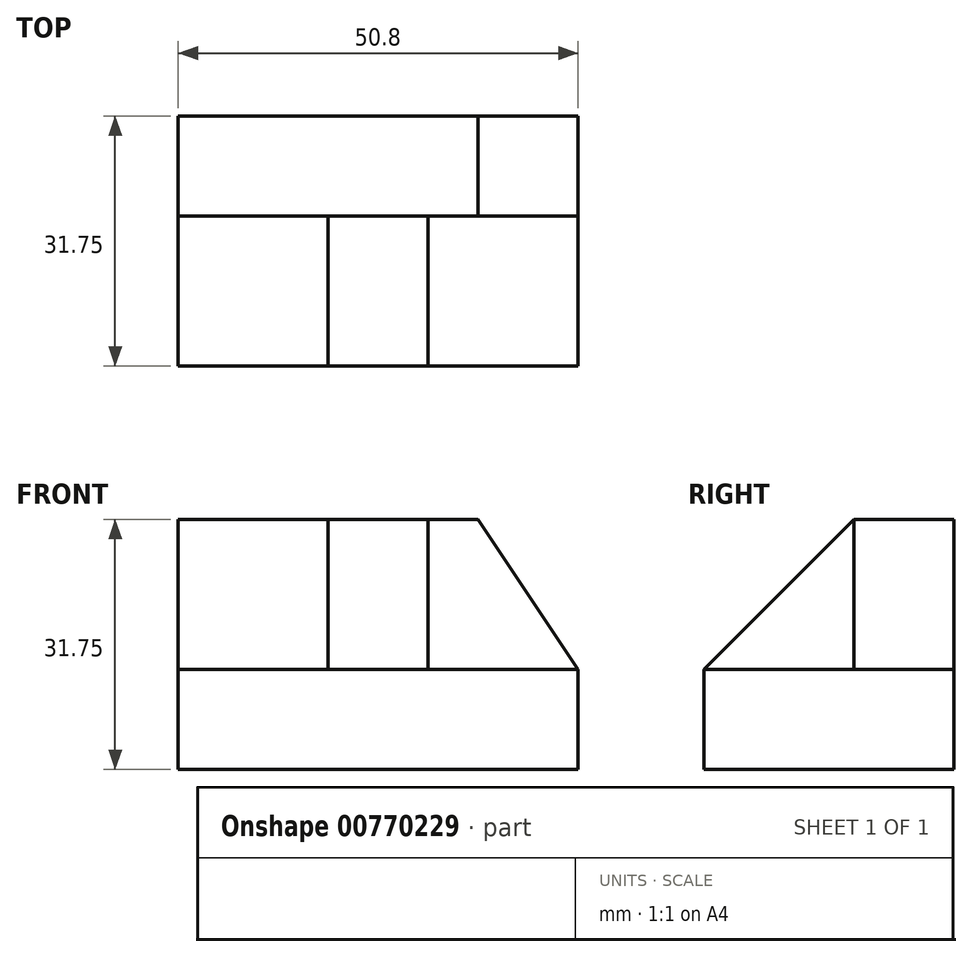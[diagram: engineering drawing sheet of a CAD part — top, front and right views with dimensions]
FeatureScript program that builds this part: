
annotation { "Feature Type Name" : "Feature", "Feature Type Description" : "" }
export const myFeature = defineFeature(function(context is Context, id is Id, definition is map)
    precondition{}
    {
        {
            var Q0;
            Q0=qCreatedBy(makeId("Front.planeOp"),FACE);
            var sketch = newSketch(context, id + "F0", { "sketchPlane" : qUnion([Q0])});
            skLineSegment(sketch, "E0", {"start": v(0, 0) * mm, "end": v(50.8, 0) * mm});
            skLineSegment(sketch, "E1", {"start": v(50.8, 0) * mm, "end": v(50.8, 31.75) * mm});
            skLineSegment(sketch, "E2", {"start": v(50.8, 31.75) * mm, "end": v(0, 31.75) * mm});
            skLineSegment(sketch, "E3", {"start": v(0, 31.75) * mm, "end": v(0, 0) * mm});
            skSolve(sketch);
        }
        {
            var Q0;
            Q0=makeQuery(id+"F0.imprint","IMPRINT",FACE,{"disambiguationData":[TD([[makeQuery(id+"F0.imprint","IMPRINT",EDGE,{"derivedFrom":sQuery(id+"F0.wireOp",EDGE,"E0")}),1.0]])]});
            extrude(context, id + "F1", {"entities" : qUnion([Q0]), "depth" : 31.75 * mm, "offsetDistance" : 25.4 * mm});
        }
        {
            var Q0;
            Q0=makeQuery(id+"F1.opExtrude","CAP_FACE",FACE,{"disambiguationData":[OSD([sQuery(id+"F0.wireOp",EDGE,"E0"),sQuery(id+"F0.wireOp",EDGE,"E1"),sQuery(id+"F0.wireOp",EDGE,"E2"),sQuery(id+"F0.wireOp",EDGE,"E3")])],"isStart":false});
            var sketch = newSketch(context, id + "F2", { "sketchPlane" : qUnion([Q0])});
            skLineSegment(sketch, "E4", {"start": v(0, 0) * mm, "end": v(0, 12.7) * mm});
            skLineSegment(sketch, "E5", {"start": v(0, 12.7) * mm, "end": v(19.05, 12.7) * mm});
            skLineSegment(sketch, "E6", {"start": v(19.05, 12.7) * mm, "end": v(19.05, 31.75) * mm});
            skLineSegment(sketch, "E7", {"start": v(19.05, 31.75) * mm, "end": v(0, 31.75) * mm});
            skLineSegment(sketch, "E8", {"start": v(0, 31.75) * mm, "end": v(0, 12.7) * mm});
            skSolve(sketch);
        }
        {
            var Q0;
            Q0=makeQuery(id+"F2.imprint","IMPRINT",FACE,{"disambiguationData":[TD([[makeQuery(id+"F2.imprint","IMPRINT",EDGE,{"derivedFrom":sQuery(id+"F2.wireOp",EDGE,"E5")}),1.0]])]});
            extrude(context, id + "F3", {"entities" : qUnion([Q0]), "operationType" : NewBodyOperationType.REMOVE, "oppositeDirection" : true, "depth" : 19.05 * mm, "offsetDistance" : 25.4 * mm});
        }
        {
            var Q0;
            Q0=makeQuery(id+"F1.opExtrude","CAP_FACE",FACE,{"disambiguationData":[OSD([sQuery(id+"F0.wireOp",EDGE,"E0"),sQuery(id+"F0.wireOp",EDGE,"E1"),sQuery(id+"F0.wireOp",EDGE,"E2"),sQuery(id+"F0.wireOp",EDGE,"E3")])],"isStart":false});
            var sketch = newSketch(context, id + "F4", { "sketchPlane" : qUnion([Q0])});
            skLineSegment(sketch, "E9", {"start": v(50.8, 12.7) * mm, "end": v(31.75, 12.7) * mm});
            skLineSegment(sketch, "E10", {"start": v(31.75, 12.7) * mm, "end": v(31.75, 31.75) * mm});
            skLineSegment(sketch, "E11", {"start": v(31.75, 31.75) * mm, "end": v(50.8, 31.75) * mm});
            skLineSegment(sketch, "E12", {"start": v(50.8, 31.75) * mm, "end": v(50.8, 12.7) * mm});
            skSolve(sketch);
        }
        {
            var Q0;
            Q0=makeQuery(id+"F4.imprint","IMPRINT",FACE,{"disambiguationData":[TD([[makeQuery(id+"F4.imprint","IMPRINT",EDGE,{"derivedFrom":sQuery(id+"F4.wireOp",EDGE,"E9")}),-1.0]])]});
            extrude(context, id + "F5", {"entities" : qUnion([Q0]), "operationType" : NewBodyOperationType.REMOVE, "oppositeDirection" : true, "depth" : 19.05 * mm, "offsetDistance" : 25.4 * mm});
        }
        {
            var Q0;
            Q0=makeQuery(id+"F5.boolean.opBoolean","COPY",FACE,{"derivedFrom":makeQuery(id+"F5.opExtrude","CAP_FACE",FACE,{"disambiguationData":[OSD([sQuery(id+"F4.wireOp",EDGE,"E9"),sQuery(id+"F4.wireOp",EDGE,"E10"),sQuery(id+"F4.wireOp",EDGE,"E11"),sQuery(id+"F4.wireOp",EDGE,"E12")])],"isStart":false})});
            var sketch = newSketch(context, id + "F6", { "sketchPlane" : qUnion([Q0])});
            skLineSegment(sketch, "E13", {"start": v(50.8, 31.75) * mm, "end": v(38.1, 31.75) * mm});
            skLineSegment(sketch, "E14", {"start": v(38.1, 31.75) * mm, "end": v(50.8, 12.7) * mm});
            skLineSegment(sketch, "E15", {"start": v(50.8, 12.7) * mm, "end": v(50.8, 31.75) * mm});
            skSolve(sketch);
        }
        {
            var Q0;
            Q0=makeQuery(id+"F6.imprint","IMPRINT",FACE,{"disambiguationData":[TD([[makeQuery(id+"F6.imprint","IMPRINT",EDGE,{"derivedFrom":sQuery(id+"F6.wireOp",EDGE,"E13")}),1.0]])]});
            extrude(context, id + "F7", {"entities" : qUnion([Q0]), "operationType" : NewBodyOperationType.REMOVE, "oppositeDirection" : true, "depth" : 25.4 * mm, "offsetDistance" : 25.4 * mm});
        }
        {
            var Q0;
            Q0=makeQuery(id+"F5.boolean.opBoolean","COPY",FACE,{"derivedFrom":makeQuery(id+"F5.opExtrude","SWEPT_FACE",FACE,{"disambiguationData":[OSD([sQuery(id+"F4.wireOp",EDGE,"E10")])]})});
            var sketch = newSketch(context, id + "F8", { "sketchPlane" : qUnion([Q0])});
            skLineSegment(sketch, "E16", {"start": v(-12.7, 31.75) * mm, "end": v(-31.75, 12.7) * mm});
            skSolve(sketch);
        }
        {
            var Q0;
            Q0=makeQuery(id+"F8.imprint","IMPRINT",FACE,{"disambiguationData":[TD([[makeQuery(id+"F8.imprint","IMPRINT",EDGE,{"derivedFrom":sQuery(id+"F8.wireOp",EDGE,"E16")}),-1.0]])]});
            extrude(context, id + "F9", {"entities" : qUnion([Q0]), "operationType" : NewBodyOperationType.REMOVE, "oppositeDirection" : true, "depth" : 25.4 * mm, "offsetDistance" : 25.4 * mm});
        }
    });
